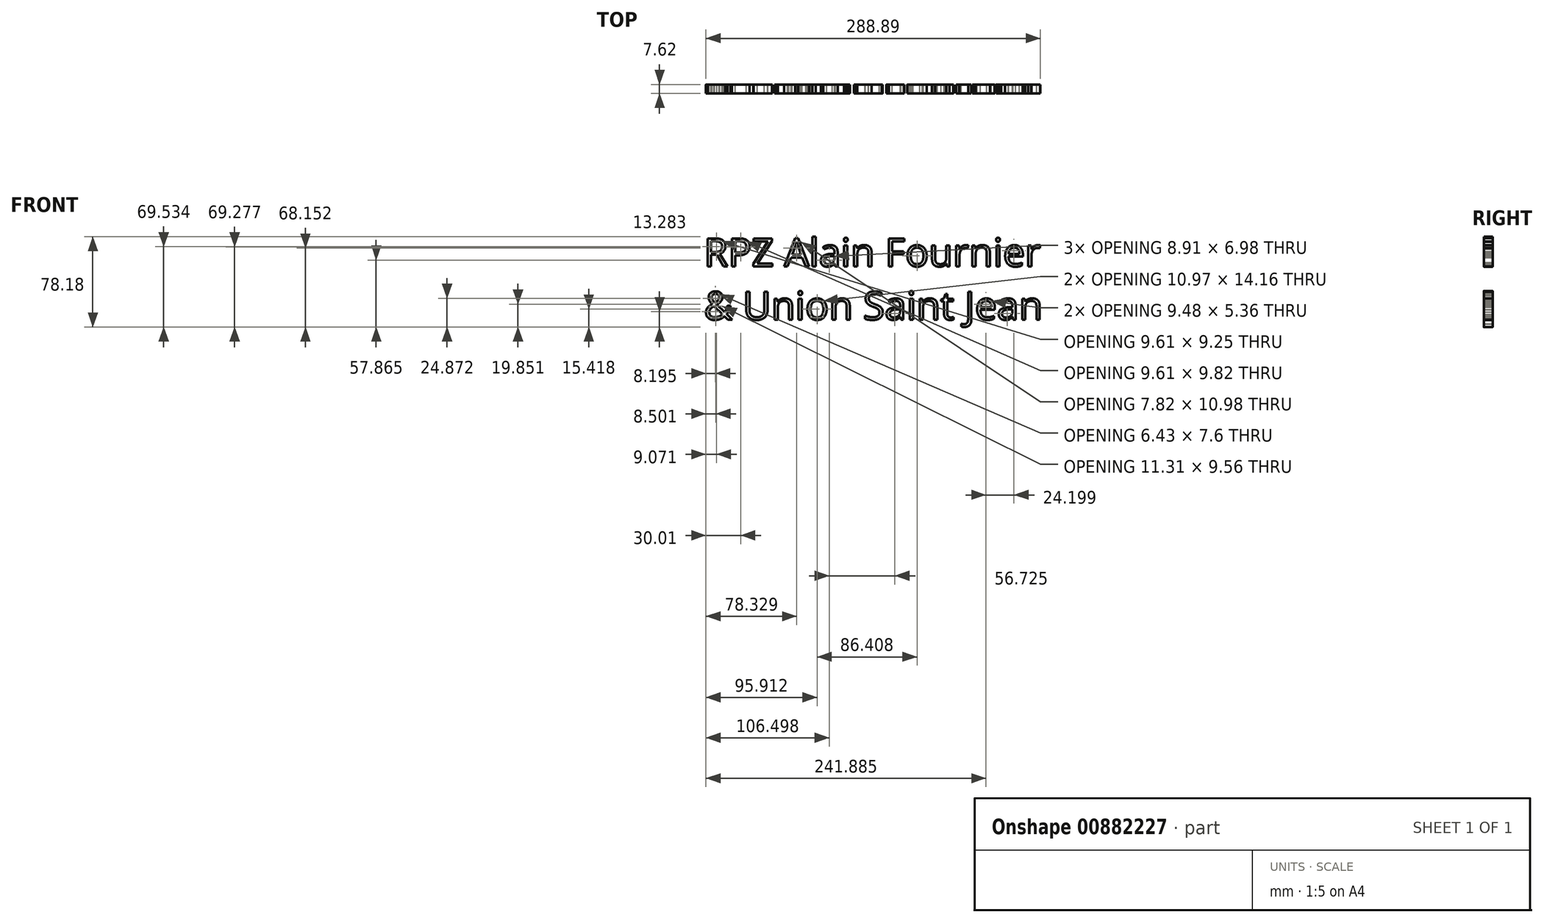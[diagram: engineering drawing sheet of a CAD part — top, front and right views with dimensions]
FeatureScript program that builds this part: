
annotation { "Feature Type Name" : "Feature", "Feature Type Description" : "" }
export const myFeature = defineFeature(function(context is Context, id is Id, definition is map)
    precondition{}
    {
        {
            var Q0;
            Q0=qCreatedBy(makeId("Front.planeOp"),FACE);
            var sketch = newSketch(context, id + "F0", { "sketchPlane" : qUnion([Q0])});
            skText(sketch, "E0", { "text": "RPZ Alain Fournier\n& Union Saint Jean", "fontName": "OpenSans-Regular.ttf"});
            const initialGuessF0  = {"E0": [-0.12542, 0.03467, 1, 0, 0.02439]};
            skSetInitialGuess(sketch, initialGuessF0);
            skSolve(sketch);
        }
        {
            var Q0;
            Q0 = qSketchRegion(id + "F0", true);
            extrude(context, id + "F1", {"entities" : qUnion([Q0]), "depth" : 7.62 * mm, "offsetDistance" : 25.4 * mm});
        }
    });
